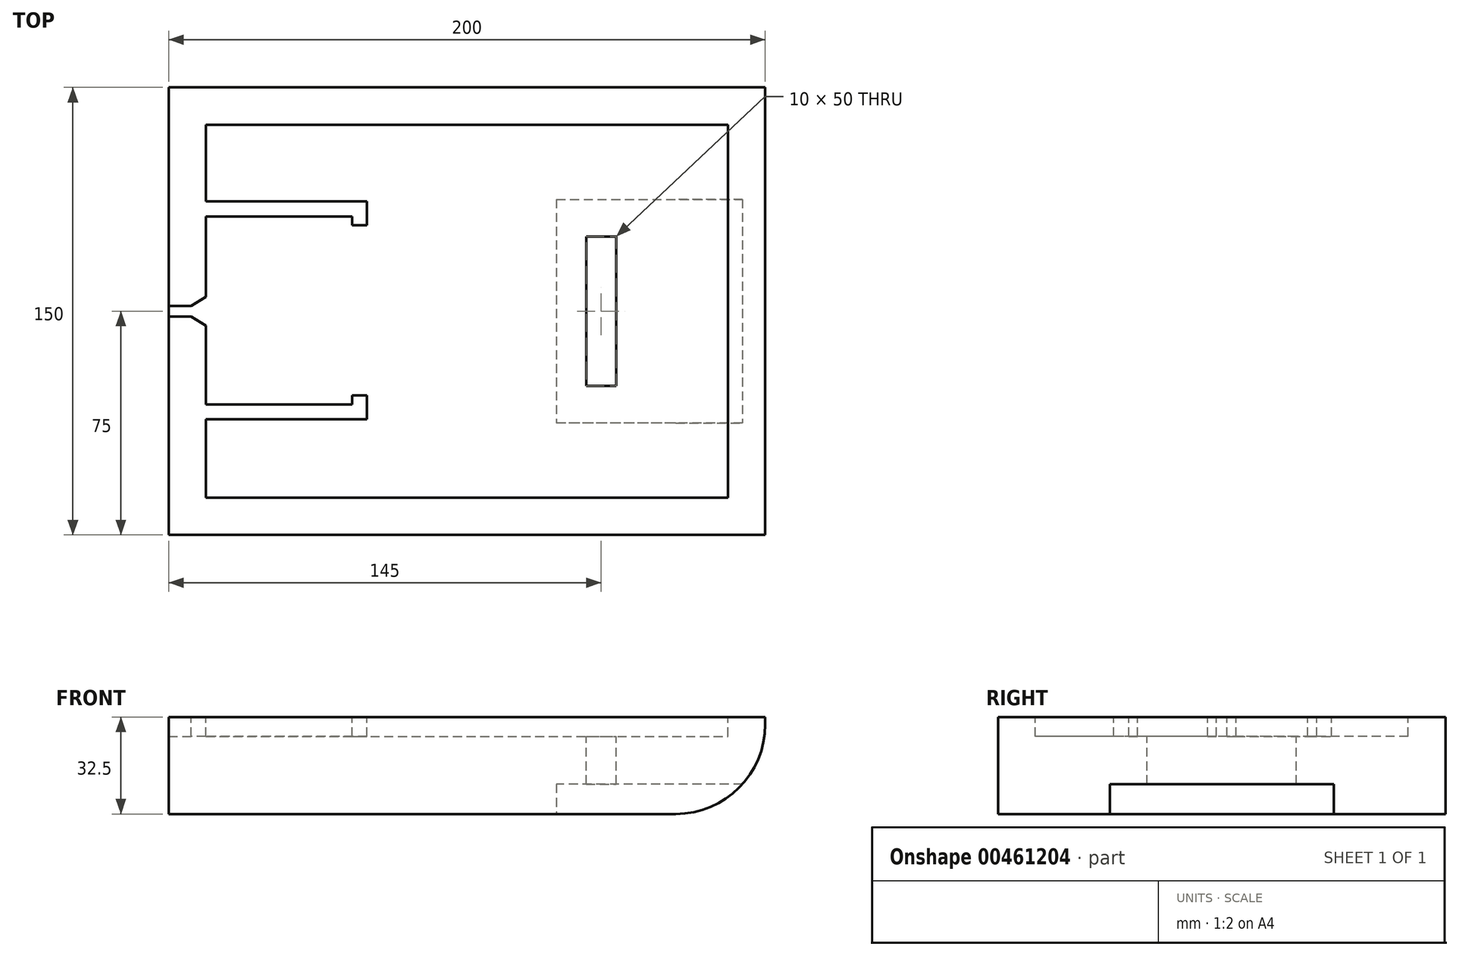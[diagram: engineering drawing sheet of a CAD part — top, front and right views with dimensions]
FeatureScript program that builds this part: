
annotation { "Feature Type Name" : "Feature", "Feature Type Description" : "" }
export const myFeature = defineFeature(function(context is Context, id is Id, definition is map)
    precondition{}
    {
        {
            var Q0;
            Q0=qCreatedBy(makeId("Front.planeOp"),FACE);
            var sketch = newSketch(context, id + "F0", { "sketchPlane" : qUnion([Q0])});
            skLineSegment(sketch, "E0.bottom", {"start": v(100, 16.25) * mm, "end": v(-100, 16.25) * mm});
            skLineSegment(sketch, "E0.top", {"start": v(70, -16.25) * mm, "end": v(-100, -16.25) * mm});
            skLineSegment(sketch, "E0.left", {"start": v(100, 16.25) * mm, "end": v(100, 13.75) * mm});
            skLineSegment(sketch, "E0.right", {"start": v(-100, 16.25) * mm, "end": v(-100, -16.25) * mm});
            skPoint(sketch, "E0.middle", {"position": v(0, 0) * mm});
            skPoint(sketch, "E1.visualSharp", {"position": v(100, -16.25) * mm});
            skArc(sketch, "E1.filletArc", {"start": v(70, -16.25) * mm, "mid": v(91.21, -7.46) * mm, "end": v(100, 13.75) * mm});
            skSolve(sketch);
        }
        {
            var Q0;
            Q0 = qSketchRegion(id + "F0", true);
            extrude(context, id + "F1", {"entities" : qUnion([Q0]), "endBound" : BoundingType.SYMMETRIC, "oppositeDirection" : true, "depth" : 150 * mm});
        }
        {
            var Q0;
            Q0=makeQuery(id+"F1.opExtrude","SWEPT_FACE",FACE,{"disambiguationData":[OSD([sQuery(id+"F0.wireOp",EDGE,"E0.bottom")])]});
            var sketch = newSketch(context, id + "F2", { "sketchPlane" : qUnion([Q0])});
            skLineSegment(sketch, "E2.bottom", {"start": v(87.5, 62.5) * mm, "end": v(-87.5, 62.5) * mm});
            skLineSegment(sketch, "E2.top", {"start": v(87.5, -62.5) * mm, "end": v(-77.5, -62.5) * mm});
            skLineSegment(sketch, "E2.left", {"start": v(87.5, 62.5) * mm, "end": v(87.5, -62.5) * mm});
            skLineSegment(sketch, "E2.right", {"start": v(-87.5, 62.5) * mm, "end": v(-87.5, 36.79) * mm});
            skPoint(sketch, "E2.middle", {"position": v(0, 0) * mm});
            skLineSegment(sketch, "E3.bottom", {"start": v(-87.5, 31.79) * mm, "end": v(-46, 31.79) * mm});
            skLineSegment(sketch, "E4", {"start": v(-46, -36.21) * mm, "end": v(-87.5, -36.21) * mm});
            skLineSegment(sketch, "E5", {"start": v(-41, -36.21) * mm, "end": v(-46, -36.21) * mm});
            skLineSegment(sketch, "E6", {"start": v(-41, 36.79) * mm, "end": v(-87.5, 36.79) * mm});
            skLineSegment(sketch, "E7.trimOffspring", {"start": v(-87.5, -36.21) * mm, "end": v(-87.5, -62.5) * mm});
            skLineSegment(sketch, "E8", {"start": v(-6, -28.21) * mm, "end": v(-6, 28.79) * mm});
            skLineSegment(sketch, "E9", {"start": v(-87.5, -62.5) * mm, "end": v(-77.5, -62.5) * mm});
            skLineSegment(sketch, "E10", {"start": v(-87.5, 31.79) * mm, "end": v(-38.5, 31.79) * mm});
            skLineSegment(sketch, "E11", {"start": v(-38.5, 31.79) * mm, "end": v(-38.5, 28.79) * mm});
            skLineSegment(sketch, "E12", {"start": v(-38.5, 28.79) * mm, "end": v(-33.5, 28.79) * mm});
            skLineSegment(sketch, "E13", {"start": v(-33.5, 28.79) * mm, "end": v(-33.5, 36.79) * mm});
            skLineSegment(sketch, "E14", {"start": v(-33.5, 36.79) * mm, "end": v(-41, 36.79) * mm});
            skLineSegment(sketch, "E15", {"start": v(-100, 1.8) * mm, "end": v(-100, -1.8) * mm});
            skLineSegment(sketch, "E16", {"start": v(-100, 1.8) * mm, "end": v(-92.5, 1.8) * mm});
            skLineSegment(sketch, "E17", {"start": v(-100, -1.8) * mm, "end": v(-92.5, -1.8) * mm});
            skLineSegment(sketch, "E18", {"start": v(-87.5, -4.8) * mm, "end": v(-92.5, -1.8) * mm});
            skLineSegment(sketch, "E19", {"start": v(-92.5, 1.8) * mm, "end": v(-87.5, 4.8) * mm});
            skLineSegment(sketch, "E20", {"start": v(-87.5, 4.8) * mm, "end": v(-87.5, 31.79) * mm});
            skLineSegment(sketch, "E21", {"start": v(-87.5, -4.8) * mm, "end": v(-87.5, -31.21) * mm});
            skLineSegment(sketch, "E22", {"start": v(-87.5, -31.21) * mm, "end": v(-38.5, -31.21) * mm});
            skLineSegment(sketch, "E23", {"start": v(-38.5, -31.21) * mm, "end": v(-38.5, -28.21) * mm});
            skLineSegment(sketch, "E24", {"start": v(-38.5, -28.21) * mm, "end": v(-33.5, -28.21) * mm});
            skLineSegment(sketch, "E25", {"start": v(-33.5, -28.21) * mm, "end": v(-33.5, -36.21) * mm});
            skLineSegment(sketch, "E26", {"start": v(-33.5, -36.21) * mm, "end": v(-41, -36.21) * mm});
            skPoint(sketch, "E27.start.orphan", {"position": v(-41, -28.21) * mm});
            skLineSegment(sketch, "E28", {"start": v(0, 0) * mm, "end": v(40, 0) * mm});
            skLineSegment(sketch, "E29", {"start": v(40, 0) * mm, "end": v(40, 37.5) * mm});
            skLineSegment(sketch, "E30", {"start": v(40, 0) * mm, "end": v(40, -37.5) * mm});
            skPoint(sketch, "E31.end.orphan", {"position": v(42.98, -37.5) * mm});
            skLineSegment(sketch, "E32", {"start": v(40, 37.5) * mm, "end": v(50, 37.5) * mm});
            skLineSegment(sketch, "E33", {"start": v(50, 37.5) * mm, "end": v(50, -37.5) * mm});
            skLineSegment(sketch, "E34", {"start": v(50, -37.5) * mm, "end": v(40, -37.5) * mm});
            skLineSegment(sketch, "E35", {"start": v(40, 0) * mm, "end": v(40, 25) * mm});
            skLineSegment(sketch, "E36", {"start": v(40, 25) * mm, "end": v(50, 25) * mm});
            skLineSegment(sketch, "E37", {"start": v(40, 0) * mm, "end": v(40, -25) * mm});
            skLineSegment(sketch, "E38", {"start": v(40, -25) * mm, "end": v(50, -25) * mm});
            skSolve(sketch);
        }
        {
            var Q0;
            Q0=makeQuery(id+"F2.imprint","IMPRINT",FACE,{"disambiguationData":[TD([[makeQuery(id+"F2.imprint","IMPRINT",EDGE,{"derivedFrom":sQuery(id+"F2.wireOp",EDGE,"E2.bottom")}),1.0]])]});
            var Q1;
            Q1=makeQuery(id+"F2.imprint","IMPRINT",FACE,{"disambiguationData":[TD([[makeQuery(id+"F2.imprint","IMPRINT",EDGE,{"derivedFrom":sQuery(id+"F2.wireOp",EDGE,"E29")}),-1.0]])]});
            var Q2;
            Q2=makeQuery(id+"F2.imprint","IMPRINT",FACE,{"disambiguationData":[TD([[makeQuery(id+"F2.imprint","IMPRINT",EDGE,{"derivedFrom":sQuery(id+"F2.wireOp",EDGE,"E30")}),1.0]])]});
            extrude(context, id + "F3", {"entities" : qUnion([Q0, Q1, Q2]), "operationType" : NewBodyOperationType.REMOVE, "oppositeDirection" : true, "depth" : 6.5 * mm, "offsetDistance" : 25 * mm});
        }
        {
            var Q0;
            Q0=makeQuery(id+"F3.boolean.opBoolean","SPLIT",FACE,{"disambiguationData":[TD([makeQuery(id+"F3.opExtrude","SWEPT_FACE",FACE,{"disambiguationData":[OSD([sQuery(id+"F2.wireOp",EDGE,"E33")])]})])],"derivedFrom":makeQuery(id+"F1.opExtrude","SWEPT_FACE",FACE,{"disambiguationData":[OSD([sQuery(id+"F0.wireOp",EDGE,"E0.bottom")])]})});
            extrude(context, id + "F4", {"entities" : qUnion([Q0]), "operationType" : NewBodyOperationType.REMOVE, "oppositeDirection" : true, "depth" : 9000 * mm, "offsetDistance" : 25 * mm});
        }
        {
            var Q0;
            Q0=makeQuery(id+"F1.opExtrude","SWEPT_FACE",FACE,{"disambiguationData":[OSD([sQuery(id+"F0.wireOp",EDGE,"E0.top")])]});
            var sketch = newSketch(context, id + "F5", { "sketchPlane" : qUnion([Q0])});
            skLineSegment(sketch, "E39", {"start": v(0, 0) * mm, "end": v(30, 0) * mm});
            skLineSegment(sketch, "E40", {"start": v(30, 0) * mm, "end": v(30, 37.5) * mm});
            skLineSegment(sketch, "E41", {"start": v(30, 0) * mm, "end": v(30, -37.5) * mm});
            skLineSegment(sketch, "E42", {"start": v(30, -37.5) * mm, "end": v(100, -37.5) * mm});
            skLineSegment(sketch, "E43", {"start": v(100, -37.5) * mm, "end": v(100, 37.5) * mm});
            skLineSegment(sketch, "E44", {"start": v(100, 37.5) * mm, "end": v(30, 37.5) * mm});
            skSolve(sketch);
        }
        {
            var Q0;
            {var subQ0=sQuery(id+"F5.wireOp",EDGE,"E43");Q0=makeQuery(id+"F5.imprint","IMPRINT",FACE,{"disambiguationData":[TD([[makeQuery(id+"F5.imprint","IMPRINT",EDGE,{"derivedFrom":subQ0}),1.0]])]});}
            var Q1;
            {var subQ7=sQuery(id+"F5.wireOp",EDGE,"E40");Q1=makeQuery(id+"F5.imprint","IMPRINT",FACE,{"disambiguationData":[TD([[makeQuery(id+"F5.imprint","IMPRINT",EDGE,{"derivedFrom":subQ7}),-1.0]])]});}
            extrude(context, id + "F6", {"entities" : qUnion([Q0, Q1]), "operationType" : NewBodyOperationType.REMOVE, "oppositeDirection" : true, "depth" : 10 * mm, "offsetDistance" : 25 * mm});
        }
    });
